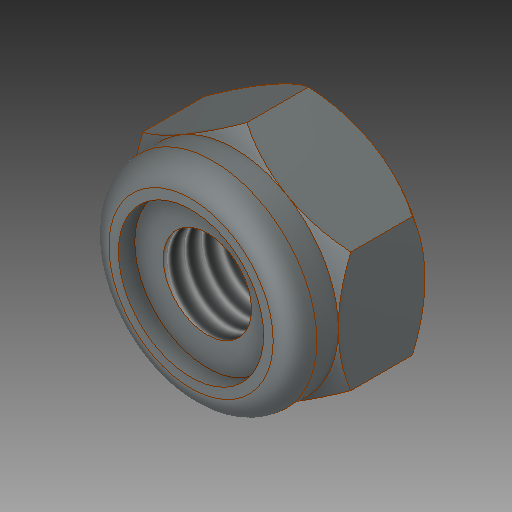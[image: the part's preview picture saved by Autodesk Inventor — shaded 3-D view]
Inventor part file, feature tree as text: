
AUTODESK INVENTOR PART (.ipt)
format: ipt  version: 2018 (Build 220112000, 112)  size: 201,728 bytes
history: native  units: in
note: dims shown in document units (in); Inventor stores cm internally (conversion verified against a paired STEP export)
features: thread x1, fillet x1
ambient origin geometry x8: Origin, YZ Plane, XZ Plane, XY Plane, X Axis, Y Axis, Z Axis, Center Point
bodies: Solid1 (feature_tree)
feature tree (2):
  thread  "Thread1"  [1 undecoded]
  fillet  "Fillet1"  [1 undecoded]
note: 2 required parameter values undecoded (feature->parameter linkage not recoverable at this tier; creation-order binding heuristic only, values carry confidence <= 0.55)
